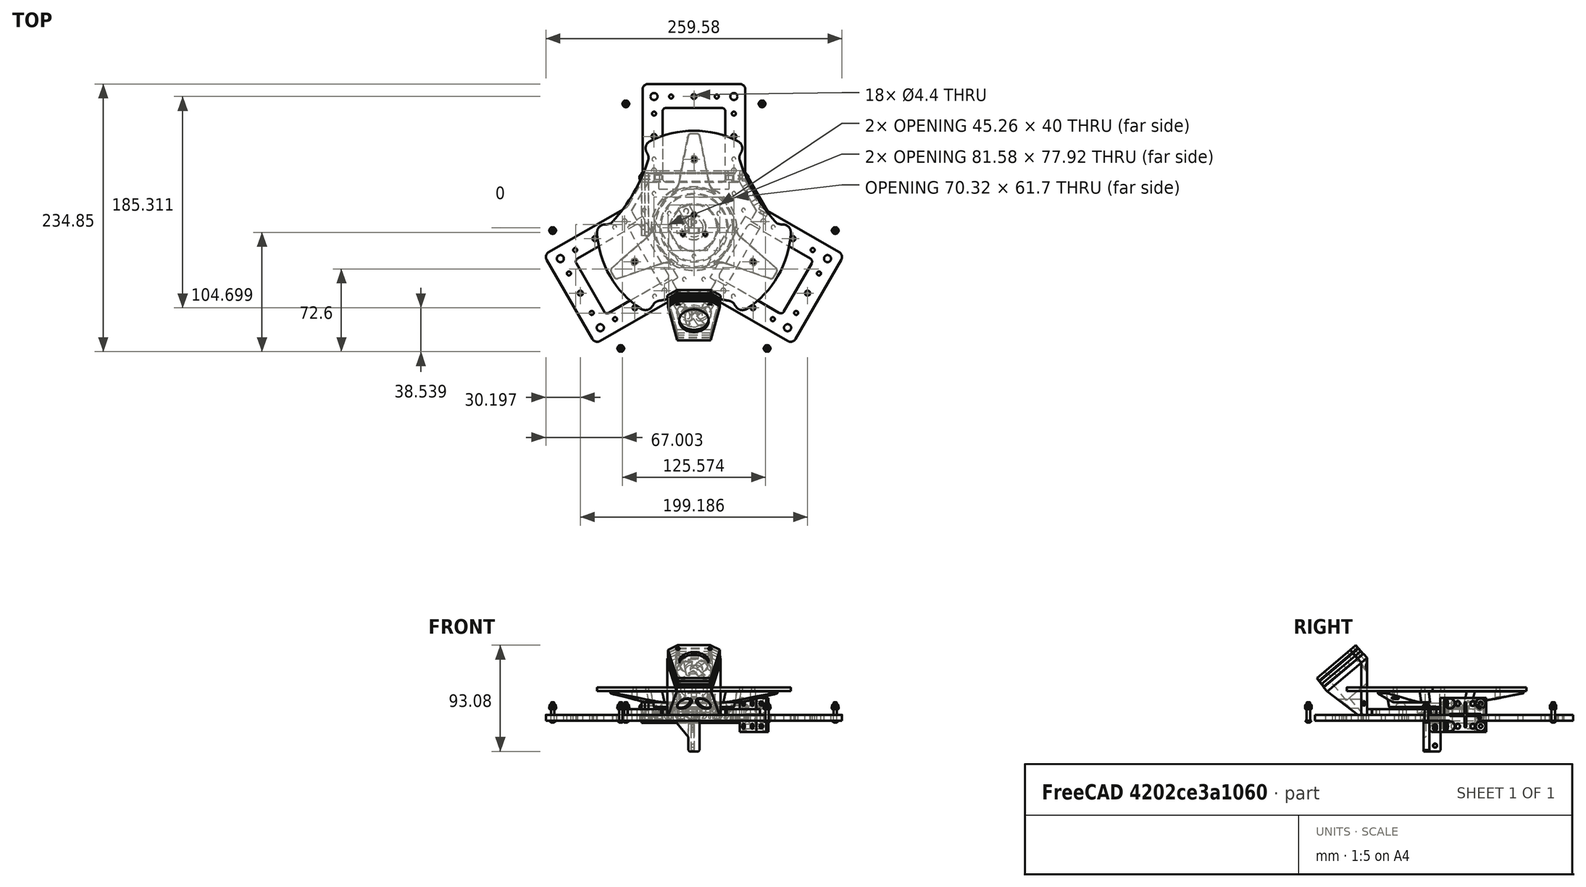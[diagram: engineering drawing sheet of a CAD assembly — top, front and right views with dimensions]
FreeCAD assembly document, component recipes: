
FREECAD ASSEMBLY — COMPONENT RECIPES ("structures")

This assembly document has 14 components, labeled P0..P13 below (a component is one placed body or linked part). 12 of them carry a construction recipe — the FreeCAD feature program that regenerates the part from scratch, quoted from this document or its linked companion documents; the rest are supplied as boundary geometry only. No exploded tour is included for this assembly.
NOTE — document 2 of 2 of this assembly tour. The two overview renders and the header above are repeated from document 1; the component sections below continue where the previous document stopped.
COMPONENT P11 — recipe-attached ("CoinTirette", modeled in this document).
Construction recipe (the document's own serialized feature program — sketch geometry with constraints, then the solid features built on it; lengths are millimeters unless a unit is written):

FEATURE [PartDesign::FeatureBase] Clone
  BaseFeature = -> Body030
  InvalidShape = false
  NewSolid = false
  Suppress = false
  TreeRank = 0
  ValidateShape = true
FEATURE [Sketcher::SketchObject] Sketch068
  ArcFitTolerance = 0
  AttachmentSupport = -> [Clone]
  ExternalBSplineMaxDegree = 0
  ExternalBSplineTolerance = 0
  ExternalGeometry = -> [Clone]
  FullyConstrained = true
  InternalTolerance = 1e-06
  InvalidShape = false
  MakeInternals = false
  MapMode = 5
  Placement = pos=(-3.09e-14,-52.3388,62.375) rot=(1,0,0;0.698132rad)
  Support = -> [Clone]
  TreeRank = 0
  ValidateShape = true
  sketch-geometry (2):
    g0: Circle CenterX=0 CenterY=-32.5627 CenterZ=0 NormalX=0 NormalY=0 NormalZ=1 AngleXU=0 Radius=3
    g1: Circle CenterX=0 CenterY=-32.5627 CenterZ=0 NormalX=0 NormalY=0 NormalZ=1 AngleXU=0 Radius=15
  constraints (4):
    c: Coincident(g0,g-3)
    c: Coincident(g1,g0)
    c: Diameter(g1) = 30
    c: Diameter(g0) = 6
FEATURE [PartDesign::Pad] Pad037
  AddSubType = 0
  AutoTaperInnerAngle = false
  BaseFeature = -> Clone
  CheckUpToFaceLimits = true
  ClaimChildren = false
  Direction = (-4e-16,-0.642788,0.766044)
  Fit = 0
  FitJoin = 0
  InnerFit = 0
  InnerFitJoin = 0
  InvalidShape = false
  Length = 10
  Length2 = 100
  Linearize = true
  NewSolid = false
  Profile = -> Sketch068
  Refine = true
  Suppress = false
  TaperInnerAngle = 0
  TaperInnerAngleRev = 0
  TreeRank = 0
  Type = 3
  UpToFace = -> Clone [Face2]
  ValidateShape = true
  _ProfileBasedVersion = 1
FEATURE [PartDesign::Body] Body032  label="PlateTirette_1"
  AutoGroupSolids = false
  BaseFeature = -> Body030
  ClaimAllChildren = false
  ExportMode = 0
  Group = -> [Clone,Sketch068,Pad037]
  InvalidShape = false
  Origin = -> Origin051
  SingleSolid = true
  Tip = -> Pad037
  TreeRank = 0
  ValidateShape = true
  _ExportChildren = -> [Clone,Pad037]
  _GroupVersion = 1
FEATURE [PartDesign::SubShapeBinder] Binder001  label="Binder001(Pad037)"
  BindCopyOnChange = 0
  BindMode = 2
  ClaimChildren = false
  Context = -> Part011 [Body033.Binder001.]
  EdgeTolerance = 1e-06
  FillStyle = 0
  Fuse = false
  InvalidShape = false
  MakeFace = true
  MergeEdges = true
  OffsetFill = false
  OffsetIntersection = false
  OffsetJoinType = 0
  OffsetOpenResult = false
  Outline = false
  PartialLoad = false
  Refine = true
  Relative = true
  SplitEdges = false
  TightBound = false
  TreeRank = 0
  ValidateShape = true
  _Version = 8
FEATURE [PartDesign::Pad] Pad038
  AddSubType = 0
  AutoTaperInnerAngle = false
  CheckUpToFaceLimits = true
  ClaimChildren = false
  Direction = (-4e-16,-0.642788,0.766044)
  Fit = 0
  FitJoin = 0
  InnerFit = 0
  InnerFitJoin = 0
  InvalidShape = false
  Length = 3
  Length2 = 100
  Linearize = true
  NewSolid = false
  Profile = -> Binder001
  Refine = true
  Suppress = false
  TaperInnerAngle = 0
  TaperInnerAngleRev = 0
  TreeRank = 0
  Type = 0
  ValidateShape = true
  _ProfileBasedVersion = 1
FEATURE [Sketcher::SketchObject] Sketch069
  ArcFitTolerance = 0
  AttachmentSupport = -> [Pad038]
  ExternalBSplineMaxDegree = 0
  ExternalBSplineTolerance = 0
  ExternalGeometry = -> [Pad038]
  FullyConstrained = true
  InternalTolerance = 1e-06
  InvalidShape = false
  MakeInternals = false
  MapMode = 5
  Placement = pos=(-3.46e-14,-54.2672,64.6731) rot=(1,0,0;0.698132rad)
  Support = -> [Pad038]
  TreeRank = 0
  ValidateShape = true
  sketch-geometry (1):
    g0: Circle CenterX=0 CenterY=-32.5627 CenterZ=0 NormalX=0 NormalY=0 NormalZ=1 AngleXU=0 Radius=12
  constraints (2):
    c: Coincident(g0,g-3)
    c: Diameter(g0) = 24
FEATURE [PartDesign::Pocket] Pocket030
  AddSubType = 1
  AutoTaperInnerAngle = false
  BaseFeature = -> Pad038
  CheckUpToFaceLimits = true
  ClaimChildren = false
  Fit = 0
  FitJoin = 0
  InnerFit = 0
  InnerFitJoin = 0
  InvalidShape = false
  Length = 5
  Length2 = 100
  Linearize = true
  NewSolid = false
  Profile = -> Sketch069
  Refine = true
  Suppress = false
  TaperInnerAngle = 0
  TaperInnerAngleRev = 0
  TreeRank = 0
  Type = 1
  ValidateShape = true
  _ProfileBasedVersion = 1
  _Version = 1
FEATURE [PartDesign::Body] Body033  label="PlateTirette_2"
  AutoGroupSolids = false
  ClaimAllChildren = false
  ExportMode = 0
  Group = -> [Binder001,Pad038,Sketch069,Pocket030]
  InvalidShape = false
  Origin = -> Origin052
  SingleSolid = true
  Tip = -> Pocket030
  TreeRank = 0
  ValidateShape = true
  _ExportChildren = -> [Pad038,Pocket030]
  _GroupVersion = 1
FEATURE [PartDesign::SubShapeBinder] Binder002  label="Binder002(Pocket030)"
  BindCopyOnChange = 0
  BindMode = 0
  ClaimChildren = false
  Context = -> Part011 [Body034.Binder002.]
  EdgeTolerance = 1e-06
  FillStyle = 0
  Fuse = false
  InvalidShape = false
  MakeFace = true
  MergeEdges = true
  OffsetFill = false
  OffsetIntersection = false
  OffsetJoinType = 0
  OffsetOpenResult = false
  Outline = false
  PartialLoad = false
  Refine = true
  Relative = true
  SplitEdges = false
  Support = -> [Body033[Pocket030.Face5]]
  TightBound = false
  TreeRank = 0
  ValidateShape = true
  _Version = 8
FEATURE [PartDesign::Pad] Pad039
  AddSubType = 0
  AutoTaperInnerAngle = false
  CheckUpToFaceLimits = true
  ClaimChildren = false
  Direction = (-4e-16,-0.642788,0.766044)
  Fit = 0
  FitJoin = 0
  InnerFit = 0
  InnerFitJoin = 0
  InvalidShape = false
  Length = 0.8
  Length2 = 100
  Linearize = true
  NewSolid = false
  Profile = -> Binder002
  Refine = true
  Suppress = false
  TaperInnerAngle = 0
  TaperInnerAngleRev = 0
  TreeRank = 0
  Type = 0
  ValidateShape = true
  _ProfileBasedVersion = 1
FEATURE [Sketcher::SketchObject] Sketch070
  ArcFitTolerance = 0
  AttachmentSupport = -> [Pad039]
  ExternalBSplineMaxDegree = 0
  ExternalBSplineTolerance = 0
  ExternalGeometry = -> [Pad039]
  FullyConstrained = true
  InternalTolerance = 1e-06
  InvalidShape = false
  MakeInternals = false
  MapMode = 5
  Placement = pos=(-3.49e-14,-54.7814,65.286) rot=(1,0,0;0.698132rad)
  Support = -> [Pad039]
  TreeRank = 0
  ValidateShape = true
  sketch-geometry (1):
    g0: Circle CenterX=0 CenterY=-32.5627 CenterZ=0 NormalX=0 NormalY=0 NormalZ=1 AngleXU=0 Radius=15
  constraints (2):
    c: Coincident(g0,g-3)
    c: Diameter(g0) = 30
FEATURE [PartDesign::Pad] Pad040
  AddSubType = 0
  AutoTaperInnerAngle = false
  BaseFeature = -> Pad039
  CheckUpToFaceLimits = true
  ClaimChildren = false
  Direction = (-4e-16,-0.642788,0.766044)
  Fit = 0
  FitJoin = 0
  InnerFit = 0
  InnerFitJoin = 0
  InvalidShape = false
  Length = 10
  Length2 = 100
  Linearize = true
  NewSolid = false
  Profile = -> Sketch070
  Refine = true
  Reversed = true
  Suppress = false
  TaperInnerAngle = 0
  TaperInnerAngleRev = 0
  TreeRank = 0
  Type = 3
  UpToFace = -> Pad039 [Face16]
  ValidateShape = true
  _ProfileBasedVersion = 1
FEATURE [PartDesign::Body] Body034  label="InterPlateTirette"
  AutoGroupSolids = false
  ClaimAllChildren = false
  ExportMode = 0
  Group = -> [Binder002,Pad039,Sketch070,Pad040]
  InvalidShape = false
  Origin = -> Origin053
  SingleSolid = true
  Tip = -> Pad040
  TreeRank = 0
  ValidateShape = true
  _ExportChildren = -> [Pad039,Pad040]
  _GroupVersion = 1
FEATURE [PartDesign::SubShapeBinder] Binder003  label="Binder003(Pad040)"
  BindCopyOnChange = 0
  BindMode = 2
  ClaimChildren = false
  Context = -> Part011 [Body035.Binder003.]
  EdgeTolerance = 1e-06
  FillStyle = 0
  Fuse = false
  InvalidShape = false
  MakeFace = true
  MergeEdges = true
  OffsetFill = false
  OffsetIntersection = false
  OffsetJoinType = 0
  OffsetOpenResult = false
  Outline = false
  PartialLoad = false
  Refine = true
  Relative = true
  SplitEdges = false
  TightBound = false
  TreeRank = 0
  ValidateShape = true
  _Version = 8
FEATURE [PartDesign::Pad] Pad041
  AddSubType = 0
  AutoTaperInnerAngle = false
  CheckUpToFaceLimits = true
  ClaimChildren = false
  Direction = (-4e-16,-0.642788,0.766044)
  Fit = 0
  FitJoin = 0
  InnerFit = 0
  InnerFitJoin = 0
  InvalidShape = false
  Length = 3
  Length2 = 100
  Linearize = true
  NewSolid = false
  Profile = -> Binder003
  Refine = true
  Suppress = false
  TaperInnerAngle = 0
  TaperInnerAngleRev = 0
  TreeRank = 0
  Type = 0
  ValidateShape = true
  _ProfileBasedVersion = 1
FEATURE [Part::SubShapeBinder] Import  label="Import(Pocket030)"
  BindCopyOnChange = 0
  BindMode = 0
  ClaimChildren = false
  Context = -> Part011 [Body035.Import.]
  EdgeTolerance = 1e-06
  FillStyle = 0
  Fuse = false
  InvalidShape = false
  MakeFace = false
  MergeEdges = true
  OffsetFill = false
  OffsetIntersection = false
  OffsetJoinType = 0
  OffsetOpenResult = false
  Outline = false
  PartialLoad = false
  Refine = true
  Relative = true
  SplitEdges = false
  Support = -> [Body033[Pocket030.]]
  TightBound = false
  TreeRank = 0
  ValidateShape = true
  _Version = 8
FEATURE [Sketcher::SketchObject] Sketch071
  ArcFitTolerance = 0
  AttachmentSupport = -> [Pad041]
  ExternalBSplineMaxDegree = 0
  ExternalBSplineTolerance = 0
  ExternalGeometry = -> [Import]
  FullyConstrained = true
  InternalTolerance = 1e-06
  InvalidShape = false
  MakeInternals = false
  MapMode = 5
  Placement = pos=(-3.62e-14,-56.7098,67.5841) rot=(1,0,0;0.698132rad)
  Support = -> [Pad041]
  TreeRank = 0
  ValidateShape = true
  sketch-geometry (2):
    g0: Circle CenterX=0 CenterY=-32.5627 CenterZ=0 NormalX=0 NormalY=0 NormalZ=1 AngleXU=0 Radius=13
    g1: LineSegment [constr] StartX=-1.96e-14 StartY=-55.0073 StartZ=0 EndX=1.98e-14 EndY=-10.1181 EndZ=0
  constraints (5):
    c: PointOnObject(g0,g-2)
    c: Diameter(g0) = 26
    c: PointOnObject(g1,g-4)
    c: Symmetric(g-3,g-3,g1)
    c: Symmetric(g1,g1,g0)
FEATURE [PartDesign::Pocket] Pocket031
  AddSubType = 1
  AutoTaperInnerAngle = false
  BaseFeature = -> Pad041
  CheckUpToFaceLimits = true
  ClaimChildren = false
  Fit = 0
  FitJoin = 0
  InnerFit = 0
  InnerFitJoin = 0
  InvalidShape = false
  Length = 5
  Length2 = 100
  Linearize = true
  NewSolid = false
  Profile = -> Sketch071
  Refine = true
  Suppress = false
  TaperInnerAngle = 0
  TaperInnerAngleRev = 0
  TreeRank = 0
  Type = 1
  ValidateShape = true
  _ProfileBasedVersion = 1
  _Version = 1
FEATURE [PartDesign::Body] Body035  label="PlateTirette_3"
  AutoGroupSolids = false
  ClaimAllChildren = false
  ExportMode = 0
  Group = -> [Binder003,Pad041,Sketch071,Import,Pocket031]
  InvalidShape = false
  Origin = -> Origin054
  SingleSolid = true
  Tip = -> Pocket031
  TreeRank = 0
  ValidateShape = true
  _ExportChildren = -> [Pad041,Import,Pocket031]
  _GroupVersion = 1
COMPONENT P12 — recipe-attached ("CoinLogo", modeled in this document).
Construction recipe (the document's own serialized feature program — sketch geometry with constraints, then the solid features built on it; lengths are millimeters unless a unit is written):

FEATURE [PartDesign::SubShapeBinder] Binder004  label="Binder004(Chamfer023)"
  BindCopyOnChange = 0
  BindMode = 0
  ClaimChildren = false
  Context = -> Part012 [Body036.Binder004.]
  EdgeTolerance = 1e-06
  FillStyle = 0
  Fuse = false
  InvalidShape = false
  MakeFace = true
  MergeEdges = true
  OffsetFill = false
  OffsetIntersection = false
  OffsetJoinType = 0
  OffsetOpenResult = false
  Outline = false
  PartialLoad = false
  Refine = true
  Relative = true
  SplitEdges = false
  Support = -> [Chamfer023[Face30]]
  TightBound = false
  TreeRank = 0
  ValidateShape = true
  _Version = 8
FEATURE [Sketcher::SketchObject] Sketch072
  ArcFitTolerance = 0
  AttachmentSupport = -> [Binder004]
  ExternalBSplineMaxDegree = 0
  ExternalBSplineTolerance = 0
  ExternalGeometry = -> [Binder004]
  FullyConstrained = true
  InternalTolerance = 1e-06
  InvalidShape = false
  MakeInternals = false
  MapMode = 5
  Placement = pos=(-2.82e-14,-50.4105,60.0769) rot=(1,0,0;0.698132rad)
  Support = -> [Binder004]
  TreeRank = 0
  ValidateShape = true
  sketch-geometry (2):
    g0: Circle CenterX=-14 CenterY=-14.7181 CenterZ=0 NormalX=0 NormalY=0 NormalZ=1 AngleXU=0 Radius=1.6
    g1: Circle CenterX=14 CenterY=-14.7181 CenterZ=0 NormalX=0 NormalY=0 NormalZ=1 AngleXU=0 Radius=1.6
  constraints (4):
    c: Coincident(g0,g-10)
    c: Coincident(g1,g-9)
    c: Diameter(g1) = 3.2
    c: Equal(g1,g0)
FEATURE [PartDesign::Pad] Pad042
  AddSubType = 0
  AutoTaperInnerAngle = false
  CheckUpToFaceLimits = true
  ClaimChildren = false
  Direction = (1,1,1)
  Fit = 0
  FitJoin = 0
  InnerFit = 0
  InnerFitJoin = 0
  InvalidShape = false
  Length = 3
  Length2 = 100
  Linearize = true
  NewSolid = false
  Profile = -> Sketch072
  Refine = true
  Suppress = false
  TaperInnerAngle = 0
  TaperInnerAngleRev = 0
  TreeRank = 0
  Type = 0
  ValidateShape = true
  _ProfileBasedVersion = 1
FEATURE [Part::Part2DObjectPython] ShapeString001  # Draft 2D object (typed FeaturePython)
  FontFile = <userpath>/Downloads/baveuse/baveuse.ttf
  InvalidShape = false
  Placement = pos=(-9,-91.52,42.09) rot=(1,0,0;0.698132rad)
  Size = 10
  String = K
  Tracking = 0
  TreeRank = 0
  ValidateShape = true
FEATURE [PartDesign::SubShapeBinder] Import001  label="Import001(ShapeString001)"
  BindCopyOnChange = 0
  BindMode = 0
  ClaimChildren = false
  Context = -> Part012 [Body036.Import001.]
  EdgeTolerance = 1e-06
  FillStyle = 0
  Fuse = false
  InvalidShape = false
  MakeFace = false
  MergeEdges = true
  OffsetFill = false
  OffsetIntersection = false
  OffsetJoinType = 0
  OffsetOpenResult = false
  Outline = false
  PartialLoad = false
  Refine = true
  Relative = true
  SplitEdges = false
  Support = -> [ShapeString001]
  TightBound = false
  TreeRank = 0
  ValidateShape = true
  _Version = 8
FEATURE [PartDesign::Pocket] Pocket032
  AddSubType = 1
  AutoTaperInnerAngle = false
  BaseFeature = -> Pad042
  CheckUpToFaceLimits = true
  ClaimChildren = false
  Fit = 0
  FitJoin = 0
  InnerFit = 0
  InnerFitJoin = 0
  InvalidShape = false
  Length = 10
  Length2 = 100
  Linearize = true
  NewSolid = false
  Profile = -> Import001
  Refine = true
  Suppress = false
  TaperInnerAngle = 0
  TaperInnerAngleRev = 0
  TreeRank = 0
  Type = 0
  ValidateShape = true
  _ProfileBasedVersion = 1
  _Version = 1
FEATURE [PartDesign::Chamfer] Chamfer024
  AddSubType = 0
  Angle = 45
  Base = -> Pocket032 [Edge48,Edge49,Edge8,Edge5,Edge1,Edge2]
  BaseFeature = -> Pocket032
  ChamferType = 0
  FlipDirection = false
  InvalidShape = false
  NewSolid = false
  Refine = true
  Size = 0.4
  Size2 = 1
  SupportTransform = false
  Suppress = false
  TreeRank = 0
  ValidateShape = true
FEATURE [PartDesign::Body] Body036  label="PlateLogo"
  AutoGroupSolids = false
  ClaimAllChildren = false
  ExportMode = 0
  Group = -> [Binder004,Sketch072,Pad042,ShapeString001,Import001,Pocket032,Chamfer024]
  InvalidShape = false
  Origin = -> Origin056
  SingleSolid = true
  Tip = -> Chamfer024
  TreeRank = 0
  ValidateShape = true
  _ExportChildren = -> [Binder004,Pad042,ShapeString001,Pocket032,Chamfer024]
  _GroupVersion = 1
FEATURE [PartDesign::FeatureBase] Clone001
  BaseFeature = -> Pad042
  InvalidShape = false
  NewSolid = false
  Suppress = false
  TreeRank = 10
  ValidateShape = true
FEATURE [Sketcher::SketchObject] Sketch073
  ArcFitTolerance = 0
  AttachmentSupport = -> [Clone001]
  ExternalBSplineMaxDegree = 0
  ExternalBSplineTolerance = 0
  ExternalGeometry = -> [Clone001]
  FullyConstrained = true
  InternalTolerance = 1e-06
  InvalidShape = false
  MakeInternals = false
  MapMode = 5
  Placement = pos=(-3.18e-14,-52.3388,62.375) rot=(1,0,0;0.698132rad)
  Support = -> [Clone001]
  TreeRank = 12
  ValidateShape = true
  sketch-geometry (1):
    g0: Circle CenterX=0 CenterY=-32.5673 CenterZ=0 NormalX=0 NormalY=0 NormalZ=1 AngleXU=0 Radius=7.5
  constraints (3):
    c: PointOnObject(g0,g-2)
    c: DistanceY(g-3,g0) = 22.44
    c: Diameter(g0) = 15
FEATURE [PartDesign::Pocket] Pocket033
  AddSubType = 1
  AutoTaperInnerAngle = false
  BaseFeature = -> Clone001
  CheckUpToFaceLimits = true
  ClaimChildren = false
  Fit = 0
  FitJoin = 0
  InnerFit = 0
  InnerFitJoin = 0
  InvalidShape = false
  Length = 5
  Length2 = 100
  Linearize = true
  NewSolid = false
  Profile = -> Sketch073
  Refine = true
  Suppress = false
  TaperInnerAngle = 0
  TaperInnerAngleRev = 0
  TreeRank = 13
  Type = 1
  ValidateShape = true
  _ProfileBasedVersion = 1
  _Version = 1
FEATURE [PartDesign::Body] Body037  label="PlateInit"
  AutoGroupSolids = false
  BaseFeature = -> Pad042
  ClaimAllChildren = false
  ExportMode = 0
  Group = -> [Clone001,Sketch073,Pocket033]
  InvalidShape = false
  Origin = -> Origin057
  SingleSolid = true
  Tip = -> Pocket033
  TreeRank = 11
  ValidateShape = true
  _ExportChildren = -> [Clone001,Pocket033]
  _GroupVersion = 1
COMPONENT P13 — recipe-attached ("RobotStand", modeled in this document).
Construction recipe (the document's own serialized feature program — sketch geometry with constraints, then the solid features built on it; lengths are millimeters unless a unit is written):

FEATURE [Sketcher::SketchObject] Sketch074
  ArcFitTolerance = 1e-06
  AttachmentSupport = -> [XY_Plane047]
  ExternalBSplineMaxDegree = 5
  ExternalBSplineTolerance = 0.0001
  FullyConstrained = true
  InternalTolerance = 1e-06
  InvalidShape = false
  MakeInternals = true
  MapMode = 5
  Support = -> [XY_Plane047]
  TreeRank = 105
  ValidateShape = true
  sketch-geometry (1):
    g0: Circle CenterX=0 CenterY=0 CenterZ=0 NormalX=0 NormalY=0 NormalZ=1 AngleXU=0 Radius=10
  constraints (2):
    c: Coincident(g0,g-1)
    c: Diameter(g0) = 20
FEATURE [PartDesign::Pad] Pad043
  AddSubType = 0
  AlongSketchNormal = false
  AutoTaperInnerAngle = true
  CheckUpToFaceLimits = true
  ClaimChildren = false
  Direction = (0,0,1)
  Fit = 0
  FitJoin = 0
  InnerFit = 0
  InnerFitJoin = 0
  InvalidShape = false
  Length = 4
  Length2 = 100
  Linearize = true
  NewSolid = false
  Profile = -> Sketch074
  Refine = true
  Suppress = false
  TaperAngle = 10
  TaperInnerAngle = -10
  TaperInnerAngleRev = 0
  TreeRank = 106
  Type = 0
  ValidateShape = true
  _ProfileBasedVersion = 1
FEATURE [PartDesign::Pad] Pad044
  AddSubType = 0
  AlongSketchNormal = false
  AutoTaperInnerAngle = true
  BaseFeature = -> Pad043
  CheckUpToFaceLimits = true
  ClaimChildren = false
  Direction = (0,0,1)
  Fit = 0
  FitJoin = 0
  InnerFit = 0
  InnerFitJoin = 0
  InvalidShape = false
  Length = 2
  Length2 = 100
  Linearize = true
  NewSolid = false
  Profile = -> Pad043 [Face3]
  Refine = true
  Suppress = false
  TaperInnerAngle = 0
  TaperInnerAngleRev = 0
  TreeRank = 107
  Type = 0
  ValidateShape = true
  _ProfileBasedVersion = 1
FEATURE [Sketcher::SketchObject] Sketch075
  ArcFitTolerance = 1e-06
  AttachmentSupport = -> [Pad044]
  ExternalBSplineMaxDegree = 5
  ExternalBSplineTolerance = 0.0001
  FullyConstrained = true
  InternalTolerance = 1e-06
  InvalidShape = false
  MakeInternals = true
  MapMode = 5
  Placement = pos=(0,0,6) rot=(0,0,1;0rad)
  Support = -> [Pad044]
  TreeRank = 108
  ValidateShape = true
  sketch-geometry (1):
    g0: Circle CenterX=0 CenterY=0 CenterZ=0 NormalX=0 NormalY=0 NormalZ=1 AngleXU=0 Radius=35
  constraints (2):
    c: Coincident(g0,g-1)
    c: Diameter(g0) = 70
FEATURE [PartDesign::Pad] Pad045
  AddSubType = 0
  AlongSketchNormal = false
  AutoTaperInnerAngle = true
  BaseFeature = -> Pad044
  CheckUpToFaceLimits = true
  ClaimChildren = false
  Direction = (0,0,1)
  Fit = 0
  FitJoin = 0
  InnerFit = 0
  InnerFitJoin = 0
  InvalidShape = false
  Length = 15
  Length2 = 100
  Linearize = true
  NewSolid = false
  Profile = -> Sketch075
  Refine = true
  Suppress = false
  TaperAngle = 10
  TaperInnerAngle = -10
  TaperInnerAngleRev = 0
  TreeRank = 109
  Type = 0
  ValidateShape = true
  _ProfileBasedVersion = 1
FEATURE [Part::SubShapeBinder] Import002  label="Import002(Fillet011)"
  BindCopyOnChange = 0
  BindMode = 0
  ClaimChildren = false
  Context = -> Group002 [Body038.Import002.]
  EdgeTolerance = 1e-06
  FillStyle = 0
  Fuse = false
  InvalidShape = false
  MakeFace = false
  MergeEdges = true
  OffsetFill = false
  OffsetIntersection = false
  OffsetJoinType = 0
  OffsetOpenResult = false
  Outline = false
  PartialLoad = false
  Relative = true
  SplitEdges = false
  Support = -> [Link075[Fillet011.]]
  TightBound = false
  TreeRank = 110
  ValidateShape = true
  _Version = 8
FEATURE [Sketcher::SketchObject] Sketch076
  ArcFitTolerance = 1e-06
  AttachmentSupport = -> [YZ_Plane047]
  ExternalBSplineMaxDegree = 5
  ExternalBSplineTolerance = 0.0001
  ExternalGeometry = -> [Pad045]
  FullyConstrained = true
  InternalTolerance = 1e-06
  InvalidShape = false
  MakeInternals = true
  MapMode = 5
  Placement = pos=(0,0,0) rot=(0.57735,0.57735,0.57735;2.0944rad)
  Support = -> [YZ_Plane047]
  TreeRank = 111
  ValidateShape = true
  sketch-geometry (5):
    g0: LineSegment StartX=21 StartY=6 StartZ=0 EndX=29 EndY=6 EndZ=0
    g1: LineSegment StartX=29 StartY=6 StartZ=0 EndX=29 EndY=10 EndZ=0
    g2: LineSegment StartX=29 StartY=10 StartZ=0 EndX=21 EndY=10 EndZ=0
    g3: LineSegment StartX=21 StartY=10 StartZ=0 EndX=21 EndY=6 EndZ=0
    g4: LineSegment [constr] StartX=25 StartY=6 StartZ=0 EndX=25 EndY=10 EndZ=0
  constraints (15):
    c: Coincident(g0,g1)
    c: Coincident(g1,g2)
    c: Coincident(g2,g3)
    c: Coincident(g3,g0)
    c: Horizontal(g0)
    c: Horizontal(g2)
    c: Vertical(g1)
    c: Vertical(g3)
    c: PointOnObject(g4,g2)
    c: Vertical(g4)
    c: Symmetric(g0,g0,g4)
    c: DistanceX(g4) = 25
    c: DistanceX(g0,g0) = 8
    c: PointOnObject(g0,g-3)
    c: DistanceY(g1,g1) = 4
FEATURE [PartDesign::Groove] Groove
  AddSubType = 1
  Angle = 360
  Axis = (-2e-16,3e-16,1)
  Base = (0,0,0)
  BaseFeature = -> Pad045
  ClaimChildren = false
  Fit = 0
  FitJoin = 0
  InnerFit = 0
  InnerFitJoin = 0
  InvalidShape = false
  Linearize = true
  NewSolid = false
  Profile = -> Sketch076
  ReferenceAxis = -> Sketch076 [V_Axis]
  Refine = true
  Suppress = false
  TreeRank = 112
  ValidateShape = true
  _ProfileBasedVersion = 1
FEATURE [Sketcher::SketchObject] Sketch077
  ArcFitTolerance = 1e-06
  AttachmentSupport = -> [Groove]
  ExternalBSplineMaxDegree = 5
  ExternalBSplineTolerance = 0.0001
  FullyConstrained = true
  InternalTolerance = 1e-06
  InvalidShape = false
  MakeInternals = true
  MapMode = 5
  Placement = pos=(0,0,21) rot=(0,0,1;0rad)
  Support = -> [Groove]
  TreeRank = 113
  ValidateShape = true
  sketch-geometry (7):
    g0: Circle CenterX=-4.7166e-12 CenterY=11.3561 CenterZ=0 NormalX=0 NormalY=0 NormalZ=1 AngleXU=0 Radius=2.2
    g1: Circle CenterX=9.83464 CenterY=-5.67803 CenterZ=0 NormalX=0 NormalY=0 NormalZ=1 AngleXU=0 Radius=2.2
    g2: Circle CenterX=-9.83464 CenterY=-5.67803 CenterZ=0 NormalX=0 NormalY=0 NormalZ=1 AngleXU=0 Radius=2.2
    g3: Circle [constr] CenterX=7.482e-13 CenterY=1.30938e-11 CenterZ=0 NormalX=0 NormalY=0 NormalZ=1 AngleXU=0 Radius=11.3561
    g4: LineSegment [constr] StartX=-9.83464 StartY=-5.67803 StartZ=0 EndX=7.478e-13 EndY=1.30935e-11 EndZ=0
    g5: LineSegment [constr] StartX=7.482e-13 StartY=1.30938e-11 StartZ=0 EndX=9.83464 EndY=-5.67803 EndZ=0
    g6: LineSegment [constr] StartX=7.482e-13 StartY=1.30938e-11 StartZ=0 EndX=-4.7166e-12 EndY=11.3561 EndZ=0
  constraints (16):
    c: PointOnObject(g0,g-2)
    c: Coincident(g3,g-1)
    c: PointOnObject(g0,g3)
    c: PointOnObject(g1,g3)
    c: PointOnObject(g2,g3)
    c: Equal(g2,g1)
    c: Equal(g1,g0)
    c: Coincident(g4,g2)
    c: Coincident(g4,g3)
    c: Coincident(g5,g3)
    c: Coincident(g5,g1)
    c: Coincident(g6,g3)
    c: Coincident(g6,g0)
    c: Angle(g5,g6) = 2.0944
    c: Symmetric(g2,g1,g-2)
    c: Diameter(g1) = 4.4
FEATURE [PartDesign::Pocket] Pocket034
  AddSubType = 1
  AutoTaperInnerAngle = true
  BaseFeature = -> Groove
  CheckUpToFaceLimits = true
  ClaimChildren = false
  Fit = 0
  FitJoin = 0
  InnerFit = 0
  InnerFitJoin = 0
  InvalidShape = false
  Length = 10
  Length2 = 100
  Linearize = true
  NewSolid = false
  Profile = -> Sketch077
  Refine = true
  Suppress = false
  TaperInnerAngle = 0
  TaperInnerAngleRev = 0
  TreeRank = 114
  Type = 0
  ValidateShape = true
  _ProfileBasedVersion = 1
  _Version = 1
FEATURE [PartDesign::Fillet] Fillet023
  AddSubType = 0
  Base = -> Pocket034 [Edge3]
  BaseFeature = -> Pocket034
  InvalidShape = false
  NewSolid = false
  Radius = 14
  Refine = true
  SupportTransform = false
  Suppress = false
  TreeRank = 115
  ValidateShape = true
FEATURE [PartDesign::Chamfer] Chamfer025
  AddSubType = 0
  Angle = 45
  Base = -> Fillet023 [Edge3]
  BaseFeature = -> Fillet023
  ChamferType = 0
  FlipDirection = false
  InvalidShape = false
  NewSolid = false
  Refine = true
  Size = 2
  Size2 = 1
  SupportTransform = false
  Suppress = false
  TreeRank = 116
  ValidateShape = true
FEATURE [PartDesign::Fillet] Fillet024
  AddSubType = 0
  Base = -> Chamfer025 [Edge13,Edge11]
  BaseFeature = -> Chamfer025
  InvalidShape = false
  NewSolid = false
  Radius = 2
  Refine = true
  SupportTransform = false
  Suppress = false
  TreeRank = 117
  ValidateShape = true
FEATURE [PartDesign::Chamfer] Chamfer026
  AddSubType = 0
  Angle = 45
  Base = -> Fillet024 [Edge18,Edge3,Edge15]
  BaseFeature = -> Fillet024
  ChamferType = 0
  FlipDirection = false
  InvalidShape = false
  NewSolid = false
  Refine = true
  Size = 1
  Size2 = 1
  SupportTransform = false
  Suppress = false
  TreeRank = 118
  ValidateShape = true
FEATURE [PartDesign::SubShapeBinder] Binder005  label="Binder005(Chamfer026)"
  BindCopyOnChange = 0
  BindMode = 0
  ClaimChildren = false
  Context = -> Group002 [Part013.Body039.Binder005.]
  EdgeTolerance = 1e-06
  FillStyle = 0
  Fuse = false
  InvalidShape = false
  MakeFace = true
  MergeEdges = true
  OffsetFill = false
  OffsetIntersection = false
  OffsetJoinType = 0
  OffsetOpenResult = false
  Outline = false
  PartialLoad = false
  Relative = true
  SplitEdges = false
  Support = -> [Body038[Chamfer026.Face17]]
  TightBound = false
  TreeRank = 133
  ValidateShape = true
  _Version = 8
FEATURE [Sketcher::SketchObject] Sketch078
  ArcFitTolerance = 1e-06
  AttachmentSupport = -> [Binder005]
  ExternalBSplineMaxDegree = 5
  ExternalBSplineTolerance = 0.0001
  FullyConstrained = true
  InternalTolerance = 1e-06
  InvalidShape = false
  MakeInternals = true
  MapMode = 5
  Placement = pos=(0,0,21) rot=(0,0,1;0rad)
  Support = -> [Binder005]
  TreeRank = 134
  ValidateShape = true
  sketch-geometry (12):
    g0: Circle CenterX=2.0355e-12 CenterY=-3.998e-13 CenterZ=0 NormalX=0 NormalY=0 NormalZ=1 AngleXU=0 Radius=85
    g1: Circle CenterX=2.0355e-12 CenterY=11.355 CenterZ=0 NormalX=0 NormalY=0 NormalZ=1 AngleXU=0 Radius=1.6
    g2: Circle CenterX=9.83372 CenterY=-5.6775 CenterZ=0 NormalX=0 NormalY=0 NormalZ=1 AngleXU=0 Radius=1.6
    g3: Circle CenterX=-9.83372 CenterY=-5.6775 CenterZ=0 NormalX=0 NormalY=0 NormalZ=1 AngleXU=0 Radius=1.6
    g4: Circle [constr] CenterX=2.0355e-12 CenterY=-3.998e-13 CenterZ=0 NormalX=0 NormalY=0 NormalZ=1 AngleXU=0 Radius=11.355
    g5: LineSegment [constr] StartX=2.0355e-12 StartY=11.355 StartZ=0 EndX=2.0355e-12 EndY=-3.997e-13 EndZ=0
    g6: LineSegment [constr] StartX=2.0355e-12 StartY=-3.998e-13 StartZ=0 EndX=-9.83372 EndY=-5.6775 EndZ=0
    g7: LineSegment [constr] StartX=2.0355e-12 StartY=-3.998e-13 StartZ=0 EndX=9.83372 EndY=-5.6775 EndZ=0
    g8: Circle CenterX=-3.78e-14 CenterY=60 CenterZ=0 NormalX=0 NormalY=0 NormalZ=1 AngleXU=0 Radius=1.6
    g9: Circle [constr] CenterX=2.0355e-12 CenterY=-3.998e-13 CenterZ=0 NormalX=0 NormalY=0 NormalZ=1 AngleXU=0 Radius=60
    g10: Circle CenterX=51.9615 CenterY=-30 CenterZ=0 NormalX=0 NormalY=0 NormalZ=1 AngleXU=0 Radius=1.6
    g11: Circle CenterX=-51.9615 CenterY=-30 CenterZ=0 NormalX=0 NormalY=0 NormalZ=1 AngleXU=0 Radius=1.6
  constraints (29):
    c: Coincident(g0,g-1)
    c: Diameter(g0) = 170
    c: Equal(g3,g2)
    c: Equal(g3,g1)
    c: Diameter(g3) = 3.2
    c: Coincident(g4,g0)
    c: PointOnObject(g1,g4)
    c: Diameter(g4) = 22.71
    c: Coincident(g5,g1)
    c: Coincident(g5,g0)
    c: Vertical(g5)
    c: Coincident(g6,g0)
    c: Coincident(g6,g3)
    c: Coincident(g7,g0)
    c: Coincident(g7,g2)
    c: Angle(g7,g5) = 2.0944
    c: Symmetric(g3,g2,g-2)
    c: PointOnObject(g2,g4)
    c: PointOnObject(g8,g-2)
    c: DistanceY(g8) = 60
    c: Equal(g8,g1)
    c: Coincident(g9,g0)
    c: PointOnObject(g8,g9)
    c: PointOnObject(g10,g9)
    c: PointOnObject(g11,g9)
    c: Equal(g11,g10)
    c: Equal(g10,g8)
    c: PointOnObject(g10,g7)
    c: PointOnObject(g11,g6)
FEATURE [PartDesign::Pad] Pad046
  AddSubType = 0
  AlongSketchNormal = false
  AutoTaperInnerAngle = true
  CheckUpToFaceLimits = true
  ClaimChildren = false
  Direction = (0,0,1)
  Fit = 0
  FitJoin = 0
  InnerFit = 0
  InnerFitJoin = 0
  InvalidShape = false
  Length = 3
  Length2 = 100
  Linearize = true
  NewSolid = false
  Profile = -> Sketch078
  Refine = true
  Suppress = false
  TaperInnerAngle = 0
  TaperInnerAngleRev = 0
  TreeRank = 135
  Type = 0
  ValidateShape = true
  _ProfileBasedVersion = 1
FEATURE [Sketcher::SketchObject] Sketch079
  ArcFitTolerance = 1e-06
  AttachmentSupport = -> [Chamfer026]
  ExternalBSplineMaxDegree = 5
  ExternalBSplineTolerance = 0.0001
  FullyConstrained = false
  InternalTolerance = 1e-06
  InvalidShape = false
  MakeInternals = true
  MapMode = 5
  Placement = pos=(0,0,21) rot=(0,0,1;0rad)
  Support = -> [Chamfer026]
  TreeRank = 136
  ValidateShape = true
  sketch-geometry (4):
    g0: ArcOfCircle CenterX=1.25182e-10 CenterY=4.9383e-12 CenterZ=0 NormalX=0 NormalY=0 NormalZ=1 AngleXU=0 Radius=34.3525 StartAngle=1.11893 EndAngle=2.02267
    g1: ArcOfCircle CenterX=1.25182e-10 CenterY=4.9383e-12 CenterZ=0 NormalX=0 NormalY=0 NormalZ=1 AngleXU=0 Radius=82.5 StartAngle=1.51015 EndAngle=1.63144
    g2: LineSegment StartX=-15 StartY=30.9046 StartZ=0 EndX=-5 EndY=82.3483 EndZ=0
    g3: LineSegment StartX=5 StartY=82.3483 StartZ=0 EndX=15 EndY=30.9046 EndZ=0
  constraints (11):
    c: Coincident(g0,g-1)
    c: Coincident(g1,g0)
    c: Symmetric(g1,g1,g-2)
    c: Symmetric(g0,g0,g-2)
    c: Coincident(g2,g0)
    c: Coincident(g2,g1)
    c: Coincident(g3,g1)
    c: Coincident(g3,g0)
    c: Diameter(g1) = 165
    c: DistanceX(g1,g1) = 10
    c: DistanceX(g0,g0) = 30
FEATURE [PartDesign::Pad] Pad047
  AddSubType = 0
  AlongSketchNormal = false
  AutoTaperInnerAngle = true
  BaseFeature = -> Chamfer026
  CheckUpToFaceLimits = true
  ClaimChildren = false
  Direction = (0,0,1)
  Fit = 0
  FitJoin = 0
  InnerFit = 0
  InnerFitJoin = 0
  InvalidShape = false
  Length = 10
  Length2 = 100
  Linearize = true
  NewSolid = false
  Profile = -> Sketch079
  Refine = true
  Reversed = true
  Suppress = false
  TaperInnerAngle = 0
  TaperInnerAngleRev = 0
  TreeRank = 137
  Type = 0
  ValidateShape = true
  _ProfileBasedVersion = 1
FEATURE [PartDesign::Chamfer] Chamfer027
  AddSubType = 0
  Angle = 45
  Base = -> Pad047 [Edge37]
  BaseFeature = -> Pad047
  ChamferType = 1
  FlipDirection = false
  InvalidShape = false
  NewSolid = false
  Refine = true
  Size = 40
  Size2 = 8
  SupportTransform = false
  Suppress = false
  TreeRank = 138
  ValidateShape = true
FEATURE [PartDesign::Fillet] Fillet025
  AddSubType = 0
  Base = -> Chamfer027 [Edge3,Edge14]
  BaseFeature = -> Chamfer027
  InvalidShape = false
  NewSolid = false
  Radius = 10
  Refine = true
  SupportTransform = false
  Suppress = false
  TreeRank = 139
  ValidateShape = true
FEATURE [PartDesign::Fillet] Fillet026
  AddSubType = 0
  Base = -> Fillet025 [Edge25,Edge5]
  BaseFeature = -> Fillet025
  InvalidShape = false
  NewSolid = false
  Radius = 3
  Refine = true
  SupportTransform = false
  Suppress = false
  TreeRank = 140
  ValidateShape = true
FEATURE [PartDesign::Fillet] Fillet027
  AddSubType = 0
  Base = -> Fillet026 [Edge7]
  BaseFeature = -> Fillet026
  InvalidShape = false
  NewSolid = false
  Radius = 40
  Refine = true
  SupportTransform = false
  Suppress = false
  TreeRank = 141
  ValidateShape = true
FEATURE [PartDesign::PolarPattern] PolarPattern
  AddSubType = 0
  Angle = 360
  Axis = -> Sketch079 [N_Axis]
  BaseFeature = -> Fillet027
  CopyShape = false
  InvalidShape = false
  NewSolid = false
  Occurrences = 3
  OriginalSubs = -> [Pad047,Chamfer027,Fillet025,Fillet026,Fillet027]
  Originals = -> [Pad047,Chamfer027,Fillet025,Fillet026,Fillet027]
  ParallelTransform = true
  Refine = true
  SubTransform = true
  Suppress = false
  TreeRank = 142
  ValidateShape = true
  _Version = 3
FEATURE [Sketcher::SketchObject] Sketch080
  ArcFitTolerance = 1e-06
  AttachmentSupport = -> [PolarPattern]
  ExternalBSplineMaxDegree = 5
  ExternalBSplineTolerance = 0.0001
  FullyConstrained = true
  InternalTolerance = 1e-06
  InvalidShape = false
  MakeInternals = true
  MapMode = 5
  Placement = pos=(0,0,21) rot=(0,0,1;0rad)
  Support = -> [PolarPattern]
  TreeRank = 143
  ValidateShape = true
  sketch-geometry (1):
    g0: Circle CenterX=0 CenterY=60 CenterZ=0 NormalX=0 NormalY=0 NormalZ=1 AngleXU=0 Radius=2.2
  constraints (3):
    c: PointOnObject(g0,g-2)
    c: Diameter(g0) = 4.4
    c: DistanceY(g-1,g0) = 60
FEATURE [PartDesign::Pocket] Pocket035
  AddSubType = 1
  AutoTaperInnerAngle = true
  BaseFeature = -> PolarPattern
  CheckUpToFaceLimits = true
  ClaimChildren = false
  Fit = 0
  FitJoin = 0
  InnerFit = 0
  InnerFitJoin = 0
  InvalidShape = false
  Length = 5
  Length2 = 100
  Linearize = true
  NewSolid = false
  Profile = -> Sketch080
  Refine = true
  Suppress = false
  TaperInnerAngle = 0
  TaperInnerAngleRev = 0
  TreeRank = 144
  Type = 1
  ValidateShape = true
  _ProfileBasedVersion = 1
  _Version = 1
FEATURE [PartDesign::PolarPattern] PolarPattern016
  AddSubType = 0
  Angle = 360
  Axis = -> Sketch080 [N_Axis]
  BaseFeature = -> Pocket035
  CopyShape = false
  InvalidShape = false
  NewSolid = false
  Occurrences = 3
  OriginalSubs = -> [Pocket035]
  Originals = -> [Pocket035]
  ParallelTransform = true
  Refine = true
  SubTransform = true
  Suppress = false
  TreeRank = 145
  ValidateShape = true
  _Version = 3
FEATURE [PartDesign::Chamfer] Chamfer028
  AddSubType = 0
  Angle = 45
  Base = -> PolarPattern016 [Edge11,Edge114,Edge108]
  BaseFeature = -> PolarPattern016
  ChamferType = 0
  FlipDirection = false
  InvalidShape = false
  NewSolid = false
  Refine = true
  Size = 1
  Size2 = 1
  SupportTransform = false
  Suppress = false
  TreeRank = 146
  ValidateShape = true
FEATURE [PartDesign::Chamfer] Chamfer029
  AddSubType = 0
  Angle = 45
  Base = -> Chamfer028 [Face11]
  BaseFeature = -> Chamfer028
  ChamferType = 0
  FlipDirection = false
  InvalidShape = false
  NewSolid = false
  Refine = true
  Size = 0.4
  Size2 = 1
  SupportTransform = false
  Suppress = false
  TreeRank = 147
  ValidateShape = true
FEATURE [PartDesign::Body] Body038  label="PlugRobot"
  AutoGroupSolids = false
  ClaimAllChildren = false
  ExportMode = 0
  Group = -> [Sketch074,Pad043,Pad044,Sketch075,Pad045,Import002,Sketch076,Groove,Sketch077,Pocket034,Fillet023,Chamfer025,Fillet024,Chamfer026,Sketch079,Pad047,Chamfer027,Fillet025,Fillet026,Fillet027,PolarPattern,Sketch080,Pocket035,PolarPattern016,Chamfer028,Chamfer029]
  InvalidShape = false
  Origin = -> Origin059
  SingleSolid = true
  Tip = -> Chamfer029
  TreeRank = 104
  ValidateShape = true
  _ExportChildren = -> [Pad043,Pad044,Pad045,Import002,Groove,Pocket034,Fillet023,Chamfer025,Fillet024,Chamfer026,Pad047,Chamfer027,Fillet025,Fillet026,Fillet027,PolarPattern,Pocket035,PolarPattern016,Chamfer028,Chamfer029]
  _GroupVersion = 1
FEATURE [Sketcher::SketchObject] Sketch081
  ArcFitTolerance = 1e-06
  AttachmentSupport = -> [Pad046]
  ExternalBSplineMaxDegree = 5
  ExternalBSplineTolerance = 0.0001
  FullyConstrained = true
  InternalTolerance = 1e-06
  InvalidShape = false
  MakeInternals = true
  MapMode = 5
  Placement = pos=(0,0,24) rot=(0,0,1;0rad)
  Support = -> [Pad046]
  TreeRank = 148
  ValidateShape = true
  sketch-geometry (6):
    g0: LineSegment StartX=-40 StartY=-75 StartZ=0 EndX=-34.2265 EndY=-65 EndZ=0
    g1: ArcOfCircle CenterX=3.0925e-12 CenterY=-211.043 CenterZ=0 NormalX=0 NormalY=0 NormalZ=1 AngleXU=0 Radius=150 StartAngle=1.34059 EndAngle=1.801
    g2: ArcOfCircle CenterX=3.8288e-12 CenterY=2.3123e-12 CenterZ=0 NormalX=0 NormalY=0 NormalZ=1 AngleXU=0 Radius=85 StartAngle=4.22243 EndAngle=5.20235
    g3: LineSegment StartX=34.2265 StartY=-65 StartZ=0 EndX=40 EndY=-75 EndZ=0
    g4: LineSegment [constr] StartX=-40 StartY=-75 StartZ=0 EndX=-8.3276e-12 EndY=-5.71797 EndZ=0
    g5: LineSegment [constr] StartX=-8.3245e-12 StartY=-5.71797 StartZ=0 EndX=40 EndY=-75 EndZ=0
  constraints (18):
    c: PointOnObject(g1,g-2)
    c: Coincident(g1,g0)
    c: Coincident(g2,g-1)
    c: Coincident(g2,g0)
    c: Coincident(g3,g1)
    c: Coincident(g3,g2)
    c: Equal(g3,g0)
    c: Angle(g0,g3) = 1.0472
    c: Diameter(g1) = 300
    c: DistanceY(g0) = -65
    c: Diameter(g2) = 170
    c: Coincident(g4,g0)
    c: PointOnObject(g4,g-2)
    c: Coincident(g5,g4)
    c: Coincident(g5,g2)
    c: PointOnObject(g1,g5)
    c: PointOnObject(g0,g4)
    c: DistanceX(g0,g2) = 80
FEATURE [PartDesign::Pocket] Pocket036
  AddSubType = 1
  AutoTaperInnerAngle = true
  BaseFeature = -> Pad046
  CheckUpToFaceLimits = true
  ClaimChildren = false
  Fit = 0
  FitJoin = 0
  InnerFit = 0
  InnerFitJoin = 0
  InvalidShape = false
  Length = 5
  Length2 = 100
  Linearize = true
  NewSolid = false
  Profile = -> Sketch081
  Refine = true
  Suppress = false
  TaperInnerAngle = 0
  TaperInnerAngleRev = 0
  TreeRank = 149
  Type = 1
  ValidateShape = true
  _ProfileBasedVersion = 1
  _Version = 1
FEATURE [PartDesign::Fillet] Fillet028
  AddSubType = 0
  Base = -> Pocket036 [Edge25,Edge14,Edge26,Edge13]
  BaseFeature = -> Pocket036
  InvalidShape = false
  NewSolid = false
  Radius = 7
  Refine = true
  SupportTransform = false
  Suppress = false
  TreeRank = 150
  ValidateShape = true
FEATURE [PartDesign::PolarPattern] PolarPattern017
  AddSubType = 0
  Angle = 360
  Axis = -> Sketch081 [N_Axis]
  BaseFeature = -> Fillet028
  CopyShape = false
  InvalidShape = false
  NewSolid = false
  Occurrences = 3
  OriginalSubs = -> [Pocket036,Fillet028]
  Originals = -> [Pocket036,Fillet028]
  ParallelTransform = true
  Refine = true
  SubTransform = true
  Suppress = false
  TreeRank = 151
  ValidateShape = true
  _Version = 3
FEATURE [PartDesign::Body] Body039  label="Plate"
  AutoGroupSolids = false
  ClaimAllChildren = false
  ExportMode = 0
  Group = -> [Binder005,Sketch078,Pad046,Sketch081,Pocket036,Fillet028,PolarPattern017]
  InvalidShape = false
  Origin = -> Origin061
  SingleSolid = true
  Tip = -> PolarPattern017
  TreeRank = 132
  ValidateShape = true
  _ExportChildren = -> [Binder005,Pad046,Pocket036,Fillet028,PolarPattern017]
  _GroupVersion = 1
PROVENANCE & LICENSES
A FreeCAD (.FCStd) document from a public repository crawl; recipes are the document's own serialized feature recipes (and, for linked parts, companion documents' recipes).
License: mit.
